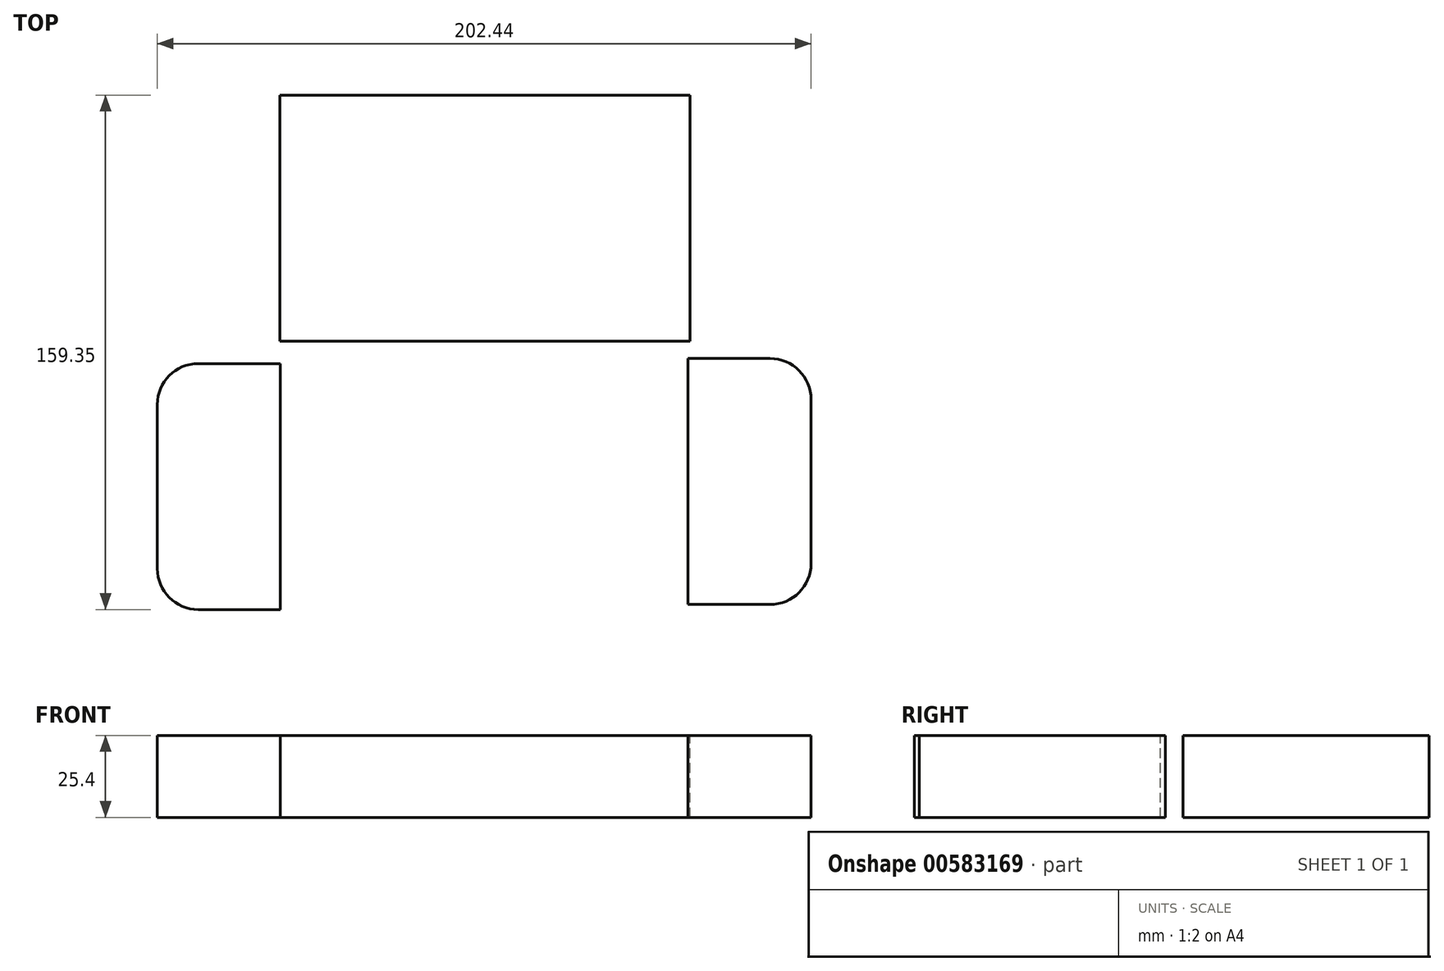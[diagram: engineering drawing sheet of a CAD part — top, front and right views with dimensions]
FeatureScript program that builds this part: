
annotation { "Feature Type Name" : "Feature", "Feature Type Description" : "" }
export const myFeature = defineFeature(function(context is Context, id is Id, definition is map)
    precondition{}
    {
        {
            var Q0;
            Q0=qCreatedBy(makeId("Top.planeOp"),FACE);
            var sketch = newSketch(context, id + "F0", { "sketchPlane" : qUnion([Q0])});
            skLineSegment(sketch, "E0.bottom", {"start": v(-8.31, 192.48) * mm, "end": v(194.89, 192.48) * mm});
            skLineSegment(sketch, "E0.top", {"start": v(-8.31, -10.72) * mm, "end": v(194.89, -10.72) * mm});
            skLineSegment(sketch, "E0.left", {"start": v(-8.31, 192.48) * mm, "end": v(-8.31, -10.72) * mm});
            skLineSegment(sketch, "E0.right", {"start": v(194.89, 192.48) * mm, "end": v(194.89, -10.72) * mm});
            skSolve(sketch);
        }
        {
            var Q0;
            Q0=makeQuery(id+"F0.imprint","IMPRINT",FACE,{"disambiguationData":[TD([[makeQuery(id+"F0.imprint","IMPRINT",EDGE,{"derivedFrom":sQuery(id+"F0.wireOp",EDGE,"E0.bottom")}),-1.0]])]});
            var sketch = newSketch(context, id + "F1", { "sketchPlane" : qUnion([Q0])});
            skLineSegment(sketch, "E1.bottom", {"start": v(30.13, 170.05) * mm, "end": v(157.13, 170.05) * mm});
            skLineSegment(sketch, "E1.top", {"start": v(30.13, 93.85) * mm, "end": v(157.13, 93.85) * mm});
            skLineSegment(sketch, "E1.left", {"start": v(30.13, 170.05) * mm, "end": v(30.13, 93.85) * mm});
            skLineSegment(sketch, "E1.right", {"start": v(157.13, 170.05) * mm, "end": v(157.13, 93.85) * mm});
            skSolve(sketch);
        }
        {
            var Q0;
            Q0=makeQuery(id+"F0.imprint","IMPRINT",FACE,{"disambiguationData":[TD([[makeQuery(id+"F0.imprint","IMPRINT",EDGE,{"derivedFrom":sQuery(id+"F0.wireOp",EDGE,"E0.bottom")}),-1.0]])]});
            var sketch = newSketch(context, id + "F2", { "sketchPlane" : qUnion([Q0])});
            skLineSegment(sketch, "E2.bottom", {"start": v(4.86, 86.9) * mm, "end": v(30.26, 86.9) * mm});
            skLineSegment(sketch, "E2.top", {"start": v(4.86, 10.7) * mm, "end": v(30.26, 10.7) * mm});
            skLineSegment(sketch, "E2.left", {"start": v(-7.84, 74.2) * mm, "end": v(-7.84, 23.4) * mm});
            skLineSegment(sketch, "E2.right", {"start": v(30.26, 86.9) * mm, "end": v(30.26, 10.7) * mm});
            skPoint(sketch, "E3.visualSharp", {"position": v(-7.84, 86.9) * mm});
            skArc(sketch, "E3.filletArc", {"start": v(4.86, 86.9) * mm, "mid": v(-4.12, 83.18) * mm, "end": v(-7.84, 74.2) * mm});
            skPoint(sketch, "E4.visualSharp", {"position": v(-7.84, 10.7) * mm});
            skArc(sketch, "E4.filletArc", {"start": v(-7.84, 23.4) * mm, "mid": v(-4.12, 14.42) * mm, "end": v(4.86, 10.7) * mm});
            skSolve(sketch);
        }
        {
            var Q0;
            Q0=makeQuery(id+"F0.imprint","IMPRINT",FACE,{"disambiguationData":[TD([[makeQuery(id+"F0.imprint","IMPRINT",EDGE,{"derivedFrom":sQuery(id+"F0.wireOp",EDGE,"E0.bottom")}),-1.0]])]});
            var sketch = newSketch(context, id + "F3", { "sketchPlane" : qUnion([Q0])});
            skLineSegment(sketch, "E5.bottom", {"start": v(156.5, 88.44) * mm, "end": v(181.9, 88.44) * mm});
            skLineSegment(sketch, "E5.top", {"start": v(156.5, 12.24) * mm, "end": v(181.9, 12.24) * mm});
            skLineSegment(sketch, "E5.left", {"start": v(156.5, 88.44) * mm, "end": v(156.5, 12.24) * mm});
            skLineSegment(sketch, "E5.right", {"start": v(194.6, 75.74) * mm, "end": v(194.6, 24.94) * mm});
            skPoint(sketch, "E6.visualSharp", {"position": v(194.6, 88.44) * mm});
            skArc(sketch, "E6.filletArc", {"start": v(194.6, 75.74) * mm, "mid": v(190.88, 84.72) * mm, "end": v(181.9, 88.44) * mm});
            skPoint(sketch, "E7.visualSharp", {"position": v(194.6, 12.24) * mm});
            skArc(sketch, "E7.filletArc", {"start": v(181.9, 12.24) * mm, "mid": v(190.88, 15.96) * mm, "end": v(194.6, 24.94) * mm});
            skSolve(sketch);
        }
        {
            var Q0;
            Q0=makeQuery(id+"F1.imprint","IMPRINT",FACE,{"disambiguationData":[TD([[makeQuery(id+"F1.imprint","IMPRINT",EDGE,{"derivedFrom":sQuery(id+"F1.wireOp",EDGE,"E1.bottom")}),-1.0]])]});
            extrude(context, id + "F4", {"entities" : qUnion([Q0]), "oppositeDirection" : true, "depth" : 25.4 * mm, "offsetDistance" : 25.4 * mm});
        }
        {
            var Q0;
            Q0=makeQuery(id+"F3.imprint","IMPRINT",FACE,{"disambiguationData":[TD([[makeQuery(id+"F3.imprint","IMPRINT",EDGE,{"derivedFrom":sQuery(id+"F3.wireOp",EDGE,"E5.bottom")}),-1.0]])]});
            extrude(context, id + "F5", {"entities" : qUnion([Q0]), "oppositeDirection" : true, "depth" : 25.4 * mm, "offsetDistance" : 25.4 * mm});
        }
        {
            var Q0;
            Q0=makeQuery(id+"F2.imprint","IMPRINT",FACE,{"disambiguationData":[TD([[makeQuery(id+"F2.imprint","IMPRINT",EDGE,{"derivedFrom":sQuery(id+"F2.wireOp",EDGE,"E2.bottom")}),-1.0]])]});
            extrude(context, id + "F6", {"entities" : qUnion([Q0]), "oppositeDirection" : true, "depth" : 25.4 * mm, "offsetDistance" : 25.4 * mm});
        }
    });
